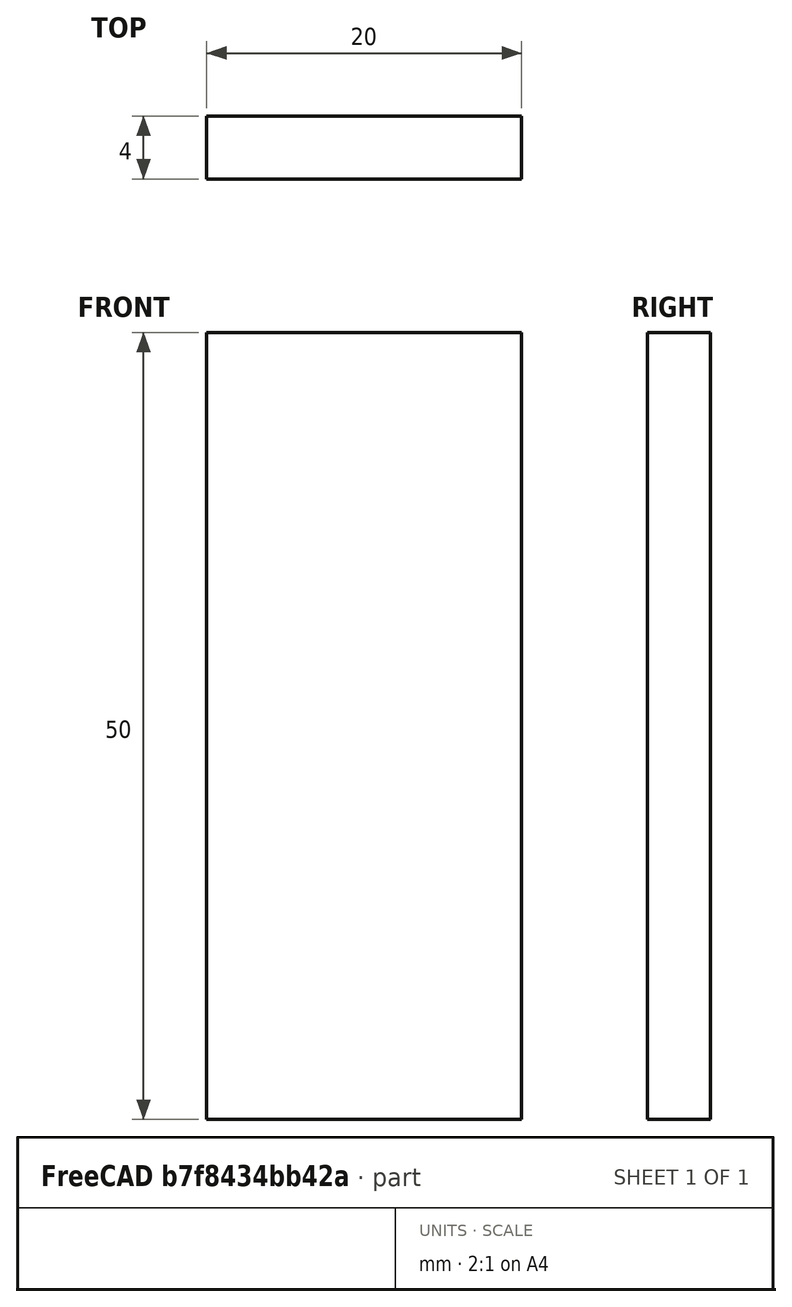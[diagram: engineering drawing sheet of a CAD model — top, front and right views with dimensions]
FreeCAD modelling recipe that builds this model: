
FCSTD DOCUMENT  (FreeCAD 0.15R4671 (Git))
Label: Flat Bar 20x4 EN10058 S235JR
License: All rights reserved
LicenseURL: http://en.wikipedia.org/wiki/All_rights_reserved
objects: Sketcher::SketchObject×1, Part::Extrusion×1
note: 2 computed .brp shape members not serialized (recipe doc carries the construction recipe); baked Part::Feature solids carry a one-line shape summary decoded from their .brp

FEATURE [Sketcher::SketchObject] Sketch
  sketch-geometry (4):
    g0: LineSegment StartX=-10 StartY=-2 StartZ=0 EndX=10 EndY=-2 EndZ=0
    g1: LineSegment StartX=10 StartY=-2 StartZ=0 EndX=10 EndY=2 EndZ=0
    g2: LineSegment StartX=10 StartY=2 StartZ=0 EndX=-10 EndY=2 EndZ=0
    g3: LineSegment StartX=-10 StartY=2 StartZ=0 EndX=-10 EndY=-2 EndZ=0
  constraints (12):
    c: Coincident(g0,g1)
    c: Coincident(g1,g2)
    c: Coincident(g2,g3)
    c: Coincident(g3,g0)
    c: Horizontal(g0)
    c: Horizontal(g2)
    c: Vertical(g1)
    c: Vertical(g3)
    c: Symmetric(g1,g2,g-2)
    c: Symmetric(g0,g1,g-1)
    c: DistanceY(g1) = 4
    c: DistanceX(g0) = 20
FEATURE [Part::Extrusion] Extrude  label="Flat Bar 20x4 EN10058 S235JR"
  Base = -> Sketch
  Dir = (0,0,50)
  Solid = true
